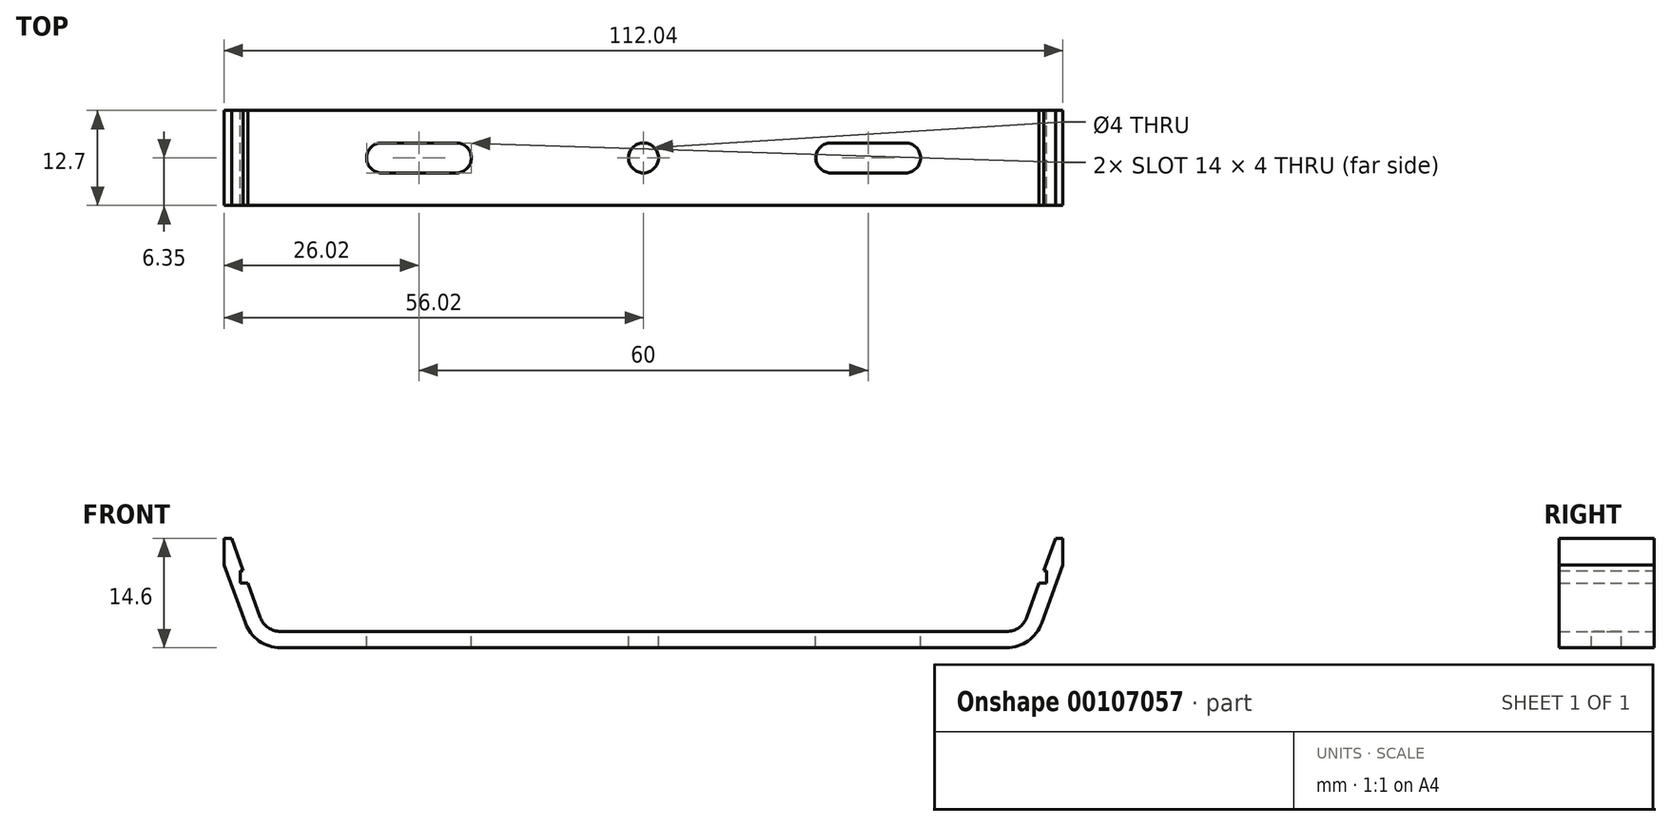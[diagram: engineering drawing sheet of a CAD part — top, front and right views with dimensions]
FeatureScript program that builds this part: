
annotation { "Feature Type Name" : "Feature", "Feature Type Description" : "" }
export const myFeature = defineFeature(function(context is Context, id is Id, definition is map)
    precondition{}
    {
        {
            var Q0;
            Q0=qCreatedBy(makeId("Front.planeOp"),FACE);
            var sketch = newSketch(context, id + "F0", { "sketchPlane" : qUnion([Q0])});
            skLineSegment(sketch, "E0", {"start": v(-50.48, 0) * mm, "end": v(50.48, 0) * mm});
            skLineSegment(sketch, "E1", {"start": v(-50.48, 0) * mm, "end": v(-55.02, 12.45) * mm});
            skLineSegment(sketch, "E2", {"start": v(-55.02, 12.45) * mm, "end": v(-56.02, 12.45) * mm});
            skLineSegment(sketch, "E3", {"start": v(-56.02, 12.45) * mm, "end": v(-56.02, 8.91) * mm});
            skLineSegment(sketch, "E4", {"start": v(-56.02, 8.91) * mm, "end": v(-51.99, -2.15) * mm});
            skLineSegment(sketch, "E5", {"start": v(-51.99, -2.15) * mm, "end": v(51.99, -2.15) * mm});
            skLineSegment(sketch, "E6", {"start": v(-53.45, 8.15) * mm, "end": v(-53.85, 8.15) * mm});
            skLineSegment(sketch, "E7", {"start": v(-53.85, 8.15) * mm, "end": v(-53.85, 6.5) * mm});
            skLineSegment(sketch, "E8", {"start": v(-53.85, 6.5) * mm, "end": v(-52.85, 6.5) * mm});
            skLineSegment(sketch, "E9", {"start": v(0, 0) * mm, "end": v(0, 48.46) * mm, "construction": true});
            skLineSegment(sketch, "E10", {"start": v(50.48, 0) * mm, "end": v(55.02, 12.45) * mm});
            skLineSegment(sketch, "E11", {"start": v(55.02, 12.45) * mm, "end": v(56.02, 12.45) * mm});
            skLineSegment(sketch, "E12", {"start": v(56.02, 12.45) * mm, "end": v(56.02, 8.91) * mm});
            skLineSegment(sketch, "E13", {"start": v(56.02, 8.91) * mm, "end": v(51.99, -2.15) * mm});
            skLineSegment(sketch, "E14", {"start": v(53.45, 8.15) * mm, "end": v(53.85, 8.15) * mm});
            skLineSegment(sketch, "E15", {"start": v(53.85, 8.15) * mm, "end": v(53.85, 6.5) * mm});
            skLineSegment(sketch, "E16", {"start": v(53.85, 6.5) * mm, "end": v(52.85, 6.5) * mm});
            skSolve(sketch);
        }
        {
            var Q0;
            {var subQ0=sQuery(id+"F0.wireOp",EDGE,"E0");Q0=makeQuery(id+"F0.imprint","IMPRINT",FACE,{"disambiguationData":[TD([[makeQuery(id+"F0.imprint","IMPRINT",EDGE,{"derivedFrom":subQ0}),-1.0]])]});}
            extrude(context, id + "F1", {"entities" : qUnion([Q0]), "endBound" : BoundingType.SYMMETRIC, "depth" : 12.7 * mm});
        }
        {
            var Q0;
            Q0=makeQuery(id+"F1.opExtrude","SWEPT_FACE",FACE,{"disambiguationData":[OSD([sQuery(id+"F0.wireOp",EDGE,"E0")])]});
            var sketch = newSketch(context, id + "F2", { "sketchPlane" : qUnion([Q0])});
            skCircle(sketch, "E17", {"center": v(0, 0) * mm, "radius": 2 * mm});
            skLineSegment(sketch, "E18", {"start": v(0, -6.35) * mm, "end": v(0, 6.35) * mm, "construction": true});
            skLineSegment(sketch, "E19", {"start": v(0, 0) * mm, "end": v(-50.48, 0) * mm, "construction": true});
            skArc(sketch, "E20", {"start": v(-25, 2) * mm, "mid": v(-23, 0) * mm, "end": v(-25, -2) * mm});
            skArc(sketch, "E21", {"start": v(-35, 2) * mm, "mid": v(-37, 0) * mm, "end": v(-35, -2) * mm});
            skLineSegment(sketch, "E22", {"start": v(-35, 2) * mm, "end": v(-25, 2) * mm});
            skLineSegment(sketch, "E23", {"start": v(-25, -2) * mm, "end": v(-35, -2) * mm});
            skLineSegment(sketch, "E24", {"start": v(0, 0) * mm, "end": v(50.48, 0) * mm, "construction": true});
            skLineSegment(sketch, "E25.bottom", {"start": v(25, 2) * mm, "end": v(35, 2) * mm});
            skLineSegment(sketch, "E25.top", {"start": v(25, -2) * mm, "end": v(35, -2) * mm});
            skLineSegment(sketch, "E25.left", {"start": v(25, 2) * mm, "end": v(25, -2) * mm, "construction": true});
            skLineSegment(sketch, "E25.right", {"start": v(35, 2) * mm, "end": v(35, -2) * mm, "construction": true});
            skPoint(sketch, "E25.middle", {"position": v(30, 0) * mm});
            skArc(sketch, "E26", {"start": v(25, 2) * mm, "mid": v(23, 0) * mm, "end": v(25, -2) * mm});
            skArc(sketch, "E27", {"start": v(35, 2) * mm, "mid": v(37, 0) * mm, "end": v(35, -2) * mm});
            skSolve(sketch);
        }
        {
            var Q0;
            Q0 = qSketchRegion(id + "F2", true);
            extrude(context, id + "F3", {"entities" : qUnion([Q0]), "operationType" : NewBodyOperationType.REMOVE, "endBound" : BoundingType.THROUGH_ALL, "oppositeDirection" : true, "depth" : 25 * mm});
        }
        {
            var Q0;
            Q0=makeQuery(id+"F1.opExtrude","SWEPT_EDGE",EDGE,{"disambiguationData":[OSD([sQuery(id+"F0.wireOp",EDGE,"E5"),sQuery(id+"F0.wireOp",EDGE,"E13")])]});
            var Q1;
            Q1=makeQuery(id+"F1.opExtrude","SWEPT_EDGE",EDGE,{"disambiguationData":[OSD([sQuery(id+"F0.wireOp",EDGE,"E4"),sQuery(id+"F0.wireOp",EDGE,"E5")])]});
            fillet(context, id + "F4", {"entities" : qUnion([Q0, Q1]), "radius" : 5 * mm, "tangentPropagation" : true, "allowEdgeOverflow" : false});
        }
        {
            var Q0;
            Q0=makeQuery(id+"F1.opExtrude","SWEPT_EDGE",EDGE,{"disambiguationData":[OSD([sQuery(id+"F0.wireOp",EDGE,"E0"),sQuery(id+"F0.wireOp",EDGE,"E10")])]});
            var Q1;
            Q1=makeQuery(id+"F1.opExtrude","SWEPT_EDGE",EDGE,{"disambiguationData":[OSD([sQuery(id+"F0.wireOp",EDGE,"E0"),sQuery(id+"F0.wireOp",EDGE,"E1")])]});
            fillet(context, id + "F5", {"entities" : qUnion([Q0, Q1]), "radius" : 2.84 * mm, "tangentPropagation" : true, "allowEdgeOverflow" : false});
        }
    });
